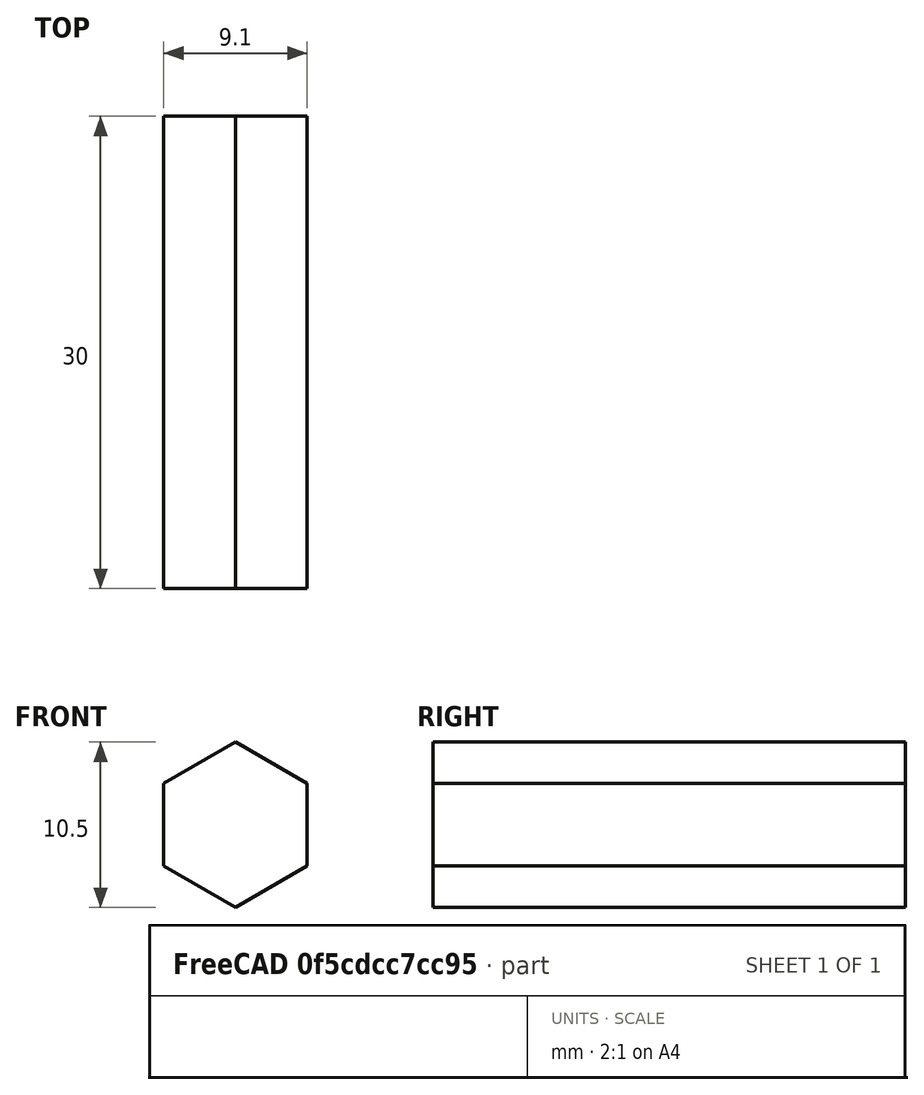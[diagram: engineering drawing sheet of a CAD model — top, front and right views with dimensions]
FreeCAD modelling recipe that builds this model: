
FCSTD DOCUMENT  (FreeCAD 1.1R44555 (Git))
Label: hex-10mm-tube
License: All rights reserved
LicenseURL: https://en.wikipedia.org/wiki/All_rights_reserved
objects: App::Point×1, Sketcher::SketchObject×1, PartDesign::Pad×1, PartDesign::Body×1
note: 6 computed .brp shape members not serialized (recipe doc carries the construction recipe); baked Part::Feature solids carry a one-line shape summary decoded from their .brp

FEATURE [App::Point] Origin001
  Role = Origin
FEATURE [Sketcher::SketchObject] Sketch
  ArcFitTolerance = 1e-06
  AttachmentSupport = -> [Origin]
  ExternalTypes = [0]
  FullyConstrained = true
  MakeInternals = false
  MapMode = 5
  Placement = pos=(0,0,0) rot=(1,0,0;1.5708rad)
  sketch-geometry (7):
    g0: LineSegment StartX=4.54663 StartY=-2.625 StartZ=0 EndX=4.54663 EndY=2.625 EndZ=0
    g1: LineSegment StartX=4.54663 StartY=2.625 StartZ=0 EndX=0 EndY=5.25 EndZ=0
    g2: LineSegment StartX=0 StartY=5.25 StartZ=0 EndX=-4.54663 EndY=2.625 EndZ=0
    g3: LineSegment StartX=-4.54663 StartY=2.625 StartZ=0 EndX=-4.54663 EndY=-2.625 EndZ=0
    g4: LineSegment StartX=-4.54663 StartY=-2.625 StartZ=0 EndX=0 EndY=-5.25 EndZ=0
    g5: LineSegment StartX=0 StartY=-5.25 StartZ=0 EndX=4.54663 EndY=-2.625 EndZ=0
    g6: Circle [constr] CenterX=0 CenterY=0 CenterZ=0 NormalX=0 NormalY=0 NormalZ=1 AngleXU=0 Radius=5.25
  constraints (16):
    c: Coincident(g0,g1)
    c: Coincident(g1,g2)
    c: Coincident(g2,g3)
    c: Coincident(g3,g4)
    c: Coincident(g4,g5)
    c: Coincident(g5,g0)
    c: Equal(g0, g1-g5) x5
    c: PointOnObject(g0,g6)
    c: PointOnObject(g1,g6)
    c: PointOnObject(g2,g6)
    c: PointOnObject(g3,g6)
    c: PointOnObject(g4,g6)
    c: PointOnObject(g5,g6)
    c: Coincident(g6,g-1)
    c: Distance(g2,g0) = 10.5
    c: PointOnObject(g1,g-2)
FEATURE [PartDesign::Pad] Pad
  Direction = (0,-1,2e-16)
  Length = 30
  Length2 = 10
  Profile = -> Sketch
  ReferenceAxis = -> Sketch [N_Axis]
  Refine = true
  SideType = 0
  Suppressed = false
  Type = 0
  Type2 = 0
FEATURE [PartDesign::Body] Body
  AllowCompound = true
  Group = -> [Sketch,Pad]
  Origin = -> Origin
  Tip = -> Pad
